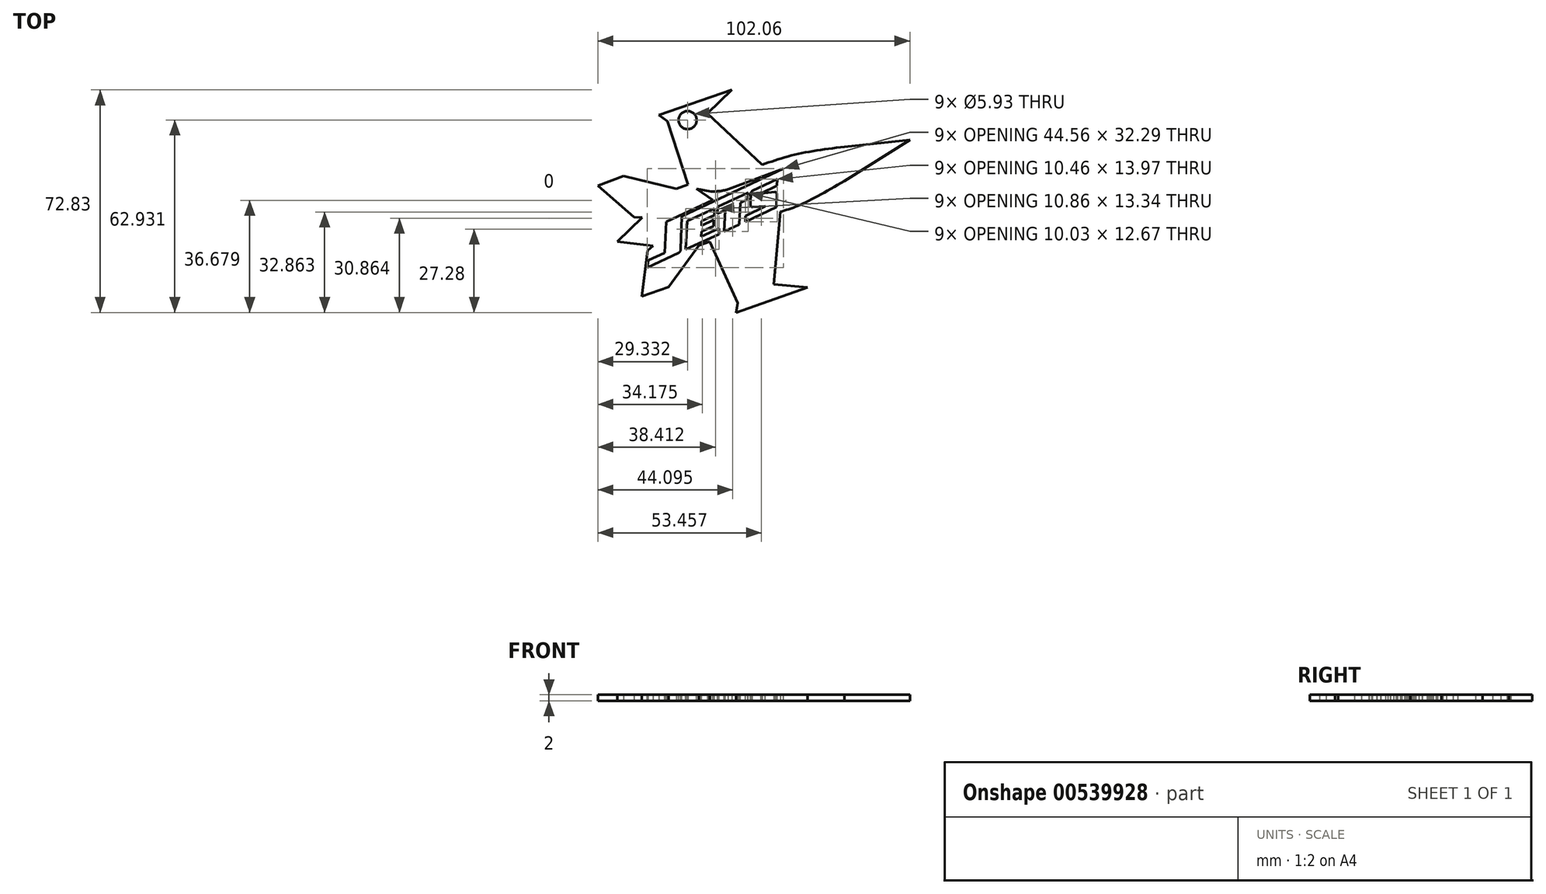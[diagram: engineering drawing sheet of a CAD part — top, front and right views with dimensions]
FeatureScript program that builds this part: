
annotation { "Feature Type Name" : "Feature", "Feature Type Description" : "" }
export const myFeature = defineFeature(function(context is Context, id is Id, definition is map)
    precondition{}
    {
        {
            var Q0;
            Q0=qCreatedBy(makeId("Top.planeOp"),FACE);
            var sketch = newSketch(context, id + "F0", { "sketchPlane" : qUnion([Q0])});
            skLineSegment(sketch, "E0", {"start": v(34.72, 5.65) * mm, "end": v(36.53, 20.6) * mm});
            skLineSegment(sketch, "E1", {"start": v(36.53, 20.6) * mm, "end": v(38.41, 22.2) * mm});
            skLineSegment(sketch, "E2", {"start": v(34.72, 5.65) * mm, "end": v(43.5, 8.73) * mm});
            skLineSegment(sketch, "E3", {"start": v(43.5, 8.73) * mm, "end": v(53.39, 22.36) * mm});
            skLineSegment(sketch, "E4", {"start": v(53.39, 22.36) * mm, "end": v(56.92, 23.6) * mm});
            skLineSegment(sketch, "E5", {"start": v(56.92, 23.6) * mm, "end": v(66.05, 3.51) * mm});
            skLineSegment(sketch, "E6", {"start": v(66.05, 3.51) * mm, "end": v(65.6, 0.37) * mm});
            skLineSegment(sketch, "E7", {"start": v(65.6, 0.37) * mm, "end": v(88.88, 8.6) * mm});
            skLineSegment(sketch, "E8", {"start": v(88.88, 8.6) * mm, "end": v(77.82, 9.6) * mm});
            skLineSegment(sketch, "E9", {"start": v(77.82, 9.6) * mm, "end": v(79.98, 33.3) * mm});
            skLineSegment(sketch, "E10", {"start": v(74.1, 48.75) * mm, "end": v(56.2, 65.49) * mm});
            skLineSegment(sketch, "E11", {"start": v(56.2, 65.49) * mm, "end": v(64.16, 73.2) * mm});
            skLineSegment(sketch, "E12", {"start": v(64.16, 73.2) * mm, "end": v(40.34, 64.96) * mm});
            skLineSegment(sketch, "E13", {"start": v(40.34, 64.96) * mm, "end": v(43.01, 62.91) * mm});
            skLineSegment(sketch, "E14", {"start": v(43.01, 62.91) * mm, "end": v(49.76, 42.2) * mm});
            skLineSegment(sketch, "E15", {"start": v(49.76, 42.2) * mm, "end": v(46.04, 40.79) * mm});
            skLineSegment(sketch, "E16", {"start": v(46.04, 40.79) * mm, "end": v(28.68, 45.04) * mm});
            skLineSegment(sketch, "E17", {"start": v(28.68, 45.04) * mm, "end": v(20.35, 41.91) * mm});
            skLineSegment(sketch, "E18", {"start": v(20.35, 41.91) * mm, "end": v(32.12, 31.55) * mm});
            skLineSegment(sketch, "E19", {"start": v(32.12, 31.55) * mm, "end": v(34.84, 31.4) * mm});
            skLineSegment(sketch, "E20", {"start": v(34.84, 31.4) * mm, "end": v(26.76, 23.56) * mm});
            skLineSegment(sketch, "E21", {"start": v(26.76, 23.56) * mm, "end": v(38.41, 22.2) * mm});
            skFitSpline(sketch, "E22", {"points": [v(74.1, 48.75) * mm, v(85.5, 52.17) * mm, v(101, 54.58) * mm], "startDerivative": vector(23.4, 8) * mm, "endDerivative": vector(30.2, 3.77) * mm});
            skLineSegment(sketch, "E23", {"start": v(101, 54.58) * mm, "end": v(122.4, 56.85) * mm});
            skLineSegment(sketch, "E24", {"start": v(122.4, 56.85) * mm, "end": v(101, 43.42) * mm});
            skFitSpline(sketch, "E25", {"points": [v(101, 43.42) * mm, v(86.71, 35.68) * mm, v(79.98, 33.3) * mm], "startDerivative": vector(-25.8, -14.97) * mm, "endDerivative": vector(-15.53, -4.56) * mm});
            skSolve(sketch);
        }
        {
            var Q0;
            Q0 = qSketchRegion(id + "F0", true);
            extrude(context, id + "F1", {"entities" : qUnion([Q0]), "depth" : 2 * mm, "offsetDistance" : 25.4 * mm});
        }
        {
            var Q0;
            Q0=makeQuery(id+"F1.opExtrude","CAP_FACE",FACE,{"disambiguationData":[OSD([sQuery(id+"F0.wireOp",EDGE,"E0"),sQuery(id+"F0.wireOp",EDGE,"E1"),sQuery(id+"F0.wireOp",EDGE,"E2"),sQuery(id+"F0.wireOp",EDGE,"E3"),sQuery(id+"F0.wireOp",EDGE,"E4"),sQuery(id+"F0.wireOp",EDGE,"E5"),sQuery(id+"F0.wireOp",EDGE,"E6"),sQuery(id+"F0.wireOp",EDGE,"E7"),sQuery(id+"F0.wireOp",EDGE,"E8"),sQuery(id+"F0.wireOp",EDGE,"E9"),sQuery(id+"F0.wireOp",EDGE,"E10"),sQuery(id+"F0.wireOp",EDGE,"E11"),sQuery(id+"F0.wireOp",EDGE,"E12"),sQuery(id+"F0.wireOp",EDGE,"E13"),sQuery(id+"F0.wireOp",EDGE,"E14"),sQuery(id+"F0.wireOp",EDGE,"E15"),sQuery(id+"F0.wireOp",EDGE,"E16"),sQuery(id+"F0.wireOp",EDGE,"E17"),sQuery(id+"F0.wireOp",EDGE,"E18"),sQuery(id+"F0.wireOp",EDGE,"E19"),sQuery(id+"F0.wireOp",EDGE,"E20"),sQuery(id+"F0.wireOp",EDGE,"E21"),sQuery(id+"F0.wireOp",EDGE,"E22"),sQuery(id+"F0.wireOp",EDGE,"E23"),sQuery(id+"F0.wireOp",EDGE,"E24"),sQuery(id+"F0.wireOp",EDGE,"E25")])],"isStart":false});
            var sketch = newSketch(context, id + "F2", { "sketchPlane" : qUnion([Q0])});
            skLineSegment(sketch, "E26", {"start": v(36.87, 17.43) * mm, "end": v(36.48, 15.09) * mm});
            skLineSegment(sketch, "E27", {"start": v(36.48, 15.09) * mm, "end": v(46.78, 19.9) * mm});
            skFitSpline(sketch, "E28", {"points": [v(46.78, 19.9) * mm, v(47.05, 20.13) * mm, v(47.27, 20.49) * mm, v(47.43, 21) * mm], "startDerivative": vector(0.95, 0.71) * mm, "endDerivative": vector(0.37, 1.47) * mm});
            skLineSegment(sketch, "E29", {"start": v(47.43, 21) * mm, "end": v(47.75, 31.86) * mm});
            skLineSegment(sketch, "E30", {"start": v(47.75, 31.86) * mm, "end": v(81.04, 47.38) * mm});
            skLineSegment(sketch, "E31", {"start": v(81.04, 47.38) * mm, "end": v(62.99, 40.68) * mm});
            skFitSpline(sketch, "E32", {"points": [v(62.99, 40.68) * mm, v(62.55, 40.56) * mm, v(61.6, 40.31) * mm, v(60.17, 40.08) * mm, v(58.66, 39.99) * mm, v(57.32, 40) * mm], "startDerivative": vector(-3.13, -0.87) * mm, "endDerivative": vector(-6, 0.09) * mm});
            skLineSegment(sketch, "E33", {"start": v(57.32, 40) * mm, "end": v(52.6, 40.8) * mm});
            skLineSegment(sketch, "E34", {"start": v(52.6, 40.8) * mm, "end": v(57.93, 37.16) * mm});
            skLineSegment(sketch, "E35", {"start": v(57.93, 37.16) * mm, "end": v(42.67, 30.04) * mm});
            skLineSegment(sketch, "E36", {"start": v(42.67, 30.04) * mm, "end": v(42.22, 19.87) * mm});
            skLineSegment(sketch, "E37", {"start": v(42.22, 19.87) * mm, "end": v(36.87, 17.43) * mm});
            skLineSegment(sketch, "E38", {"start": v(49.1, 20.98) * mm, "end": v(49.5, 30.24) * mm});
            skLineSegment(sketch, "E39", {"start": v(49.5, 30.24) * mm, "end": v(58.45, 34.32) * mm});
            skLineSegment(sketch, "E40", {"start": v(58.45, 34.32) * mm, "end": v(58.4, 32.26) * mm});
            skLineSegment(sketch, "E41", {"start": v(58.4, 32.26) * mm, "end": v(54.3, 30.34) * mm});
            skLineSegment(sketch, "E42", {"start": v(54.3, 30.34) * mm, "end": v(54.25, 28.8) * mm});
            skLineSegment(sketch, "E43", {"start": v(54.25, 28.8) * mm, "end": v(58.25, 30.63) * mm});
            skLineSegment(sketch, "E44", {"start": v(58.25, 30.63) * mm, "end": v(58.16, 28.68) * mm});
            skLineSegment(sketch, "E45", {"start": v(58.16, 28.68) * mm, "end": v(54.22, 26.84) * mm});
            skLineSegment(sketch, "E46", {"start": v(54.22, 26.84) * mm, "end": v(54.15, 25.25) * mm});
            skLineSegment(sketch, "E47", {"start": v(54.15, 25.25) * mm, "end": v(59.95, 27.9) * mm});
            skLineSegment(sketch, "E48", {"start": v(59.95, 27.9) * mm, "end": v(59.9, 26.01) * mm});
            skLineSegment(sketch, "E49", {"start": v(59.9, 26.01) * mm, "end": v(49.1, 20.98) * mm});
            skLineSegment(sketch, "E50", {"start": v(59.43, 32.81) * mm, "end": v(59.52, 34.93) * mm});
            skLineSegment(sketch, "E51", {"start": v(59.52, 34.93) * mm, "end": v(69.46, 39.57) * mm});
            skLineSegment(sketch, "E52", {"start": v(69.46, 39.57) * mm, "end": v(69.36, 37.38) * mm});
            skLineSegment(sketch, "E53", {"start": v(69.36, 37.38) * mm, "end": v(66.91, 36.23) * mm});
            skLineSegment(sketch, "E54", {"start": v(66.91, 36.23) * mm, "end": v(66.6, 29.14) * mm});
            skLineSegment(sketch, "E55", {"start": v(66.6, 29.14) * mm, "end": v(61.67, 26.9) * mm});
            skLineSegment(sketch, "E56", {"start": v(61.67, 26.9) * mm, "end": v(61.98, 33.9) * mm});
            skLineSegment(sketch, "E57", {"start": v(61.98, 33.9) * mm, "end": v(59.46, 32.74) * mm});
            skLineSegment(sketch, "E58", {"start": v(59.46, 32.74) * mm, "end": v(59.43, 32.81) * mm});
            skLineSegment(sketch, "E59", {"start": v(68.58, 30.06) * mm, "end": v(68.63, 31.95) * mm});
            skLineSegment(sketch, "E60", {"start": v(68.63, 31.95) * mm, "end": v(75.05, 35.18) * mm});
            skLineSegment(sketch, "E61", {"start": v(75.05, 35.18) * mm, "end": v(70.95, 34.82) * mm});
            skFitSpline(sketch, "E62", {"points": [v(70.95, 34.82) * mm, v(70.66, 34.91) * mm, v(70.33, 35.18) * mm, v(70.23, 35.63) * mm, v(70.3, 36.23) * mm], "startDerivative": vector(-1.36, 0.33) * mm, "endDerivative": vector(0.28, 2.12) * mm});
            skLineSegment(sketch, "E63", {"start": v(70.3, 36.23) * mm, "end": v(70.37, 39.36) * mm});
            skFitSpline(sketch, "E64", {"points": [v(70.37, 39.36) * mm, v(70.44, 39.56) * mm, v(70.54, 39.83) * mm, v(70.81, 40.12) * mm, v(70.94, 40.26) * mm], "startDerivative": vector(0.31, 0.87) * mm, "endDerivative": vector(0.53, 0.6) * mm});
            skLineSegment(sketch, "E65", {"start": v(70.94, 40.26) * mm, "end": v(79.04, 44.03) * mm});
            skLineSegment(sketch, "E66", {"start": v(79.04, 44.03) * mm, "end": v(78.85, 41.8) * mm});
            skLineSegment(sketch, "E67", {"start": v(78.85, 41.8) * mm, "end": v(73.63, 39.37) * mm});
            skLineSegment(sketch, "E68", {"start": v(73.63, 39.37) * mm, "end": v(78.27, 39.8) * mm});
            skFitSpline(sketch, "E69", {"points": [v(78.27, 39.8) * mm, v(78.6, 39.66) * mm, v(78.81, 39.44) * mm, v(78.83, 39.29) * mm, v(78.84, 38.9) * mm], "startDerivative": vector(1.28, -0.35) * mm, "endDerivative": vector(0.02, -1.52) * mm});
            skLineSegment(sketch, "E70", {"start": v(78.84, 38.9) * mm, "end": v(78.78, 34.82) * mm});
            skLineSegment(sketch, "E71", {"start": v(78.78, 34.82) * mm, "end": v(68.58, 30.06) * mm});
            skLineSegment(sketch, "E72.0", {"start": v(49.1, 20.98) * mm, "end": v(78.78, 34.82) * mm, "construction": true});
            skLineSegment(sketch, "E73.0", {"start": v(69.46, 39.57) * mm, "end": v(70.94, 40.26) * mm, "construction": true});
            skLineSegment(sketch, "E74.0", {"start": v(42.22, 19.87) * mm, "end": v(75.05, 35.18) * mm, "construction": true});
            skLineSegment(sketch, "E75.0", {"start": v(59.95, 27.9) * mm, "end": v(68.63, 31.95) * mm, "construction": true});
            skLineSegment(sketch, "E76.0", {"start": v(70.95, 34.82) * mm, "end": v(70.3, 36.23) * mm, "construction": true});
            skLineSegment(sketch, "E77.0", {"start": v(59.46, 32.74) * mm, "end": v(59.43, 32.81) * mm, "construction": true});
            skSolve(sketch);
        }
        {
            var Q0;
            Q0 = qSketchRegion(id + "F2", true);
            extrude(context, id + "F3", {"entities" : qUnion([Q0]), "operationType" : NewBodyOperationType.REMOVE, "oppositeDirection" : true, "depth" : 25.4 * mm, "offsetDistance" : 25.4 * mm});
        }
        {
            var Q0;
            Q0=makeQuery(id+"F1.opExtrude","CAP_FACE",FACE,{"disambiguationData":[OSD([sQuery(id+"F0.wireOp",EDGE,"E0"),sQuery(id+"F0.wireOp",EDGE,"E1"),sQuery(id+"F0.wireOp",EDGE,"E2"),sQuery(id+"F0.wireOp",EDGE,"E3"),sQuery(id+"F0.wireOp",EDGE,"E4"),sQuery(id+"F0.wireOp",EDGE,"E5"),sQuery(id+"F0.wireOp",EDGE,"E6"),sQuery(id+"F0.wireOp",EDGE,"E7"),sQuery(id+"F0.wireOp",EDGE,"E8"),sQuery(id+"F0.wireOp",EDGE,"E9"),sQuery(id+"F0.wireOp",EDGE,"E10"),sQuery(id+"F0.wireOp",EDGE,"E11"),sQuery(id+"F0.wireOp",EDGE,"E12"),sQuery(id+"F0.wireOp",EDGE,"E13"),sQuery(id+"F0.wireOp",EDGE,"E14"),sQuery(id+"F0.wireOp",EDGE,"E15"),sQuery(id+"F0.wireOp",EDGE,"E16"),sQuery(id+"F0.wireOp",EDGE,"E17"),sQuery(id+"F0.wireOp",EDGE,"E18"),sQuery(id+"F0.wireOp",EDGE,"E19"),sQuery(id+"F0.wireOp",EDGE,"E20"),sQuery(id+"F0.wireOp",EDGE,"E21"),sQuery(id+"F0.wireOp",EDGE,"E22"),sQuery(id+"F0.wireOp",EDGE,"E23"),sQuery(id+"F0.wireOp",EDGE,"E24"),sQuery(id+"F0.wireOp",EDGE,"E25")])],"isStart":false});
            var sketch = newSketch(context, id + "F4", { "sketchPlane" : qUnion([Q0])});
            skCircle(sketch, "E78", {"center": v(49.68, 63.3) * mm, "radius": 2.97 * mm});
            skSolve(sketch);
        }
        {
            var Q0;
            Q0 = qSketchRegion(id + "F4", true);
            extrude(context, id + "F5", {"entities" : qUnion([Q0]), "operationType" : NewBodyOperationType.REMOVE, "oppositeDirection" : true, "depth" : 25.4 * mm, "offsetDistance" : 25.4 * mm});
        }
    });
